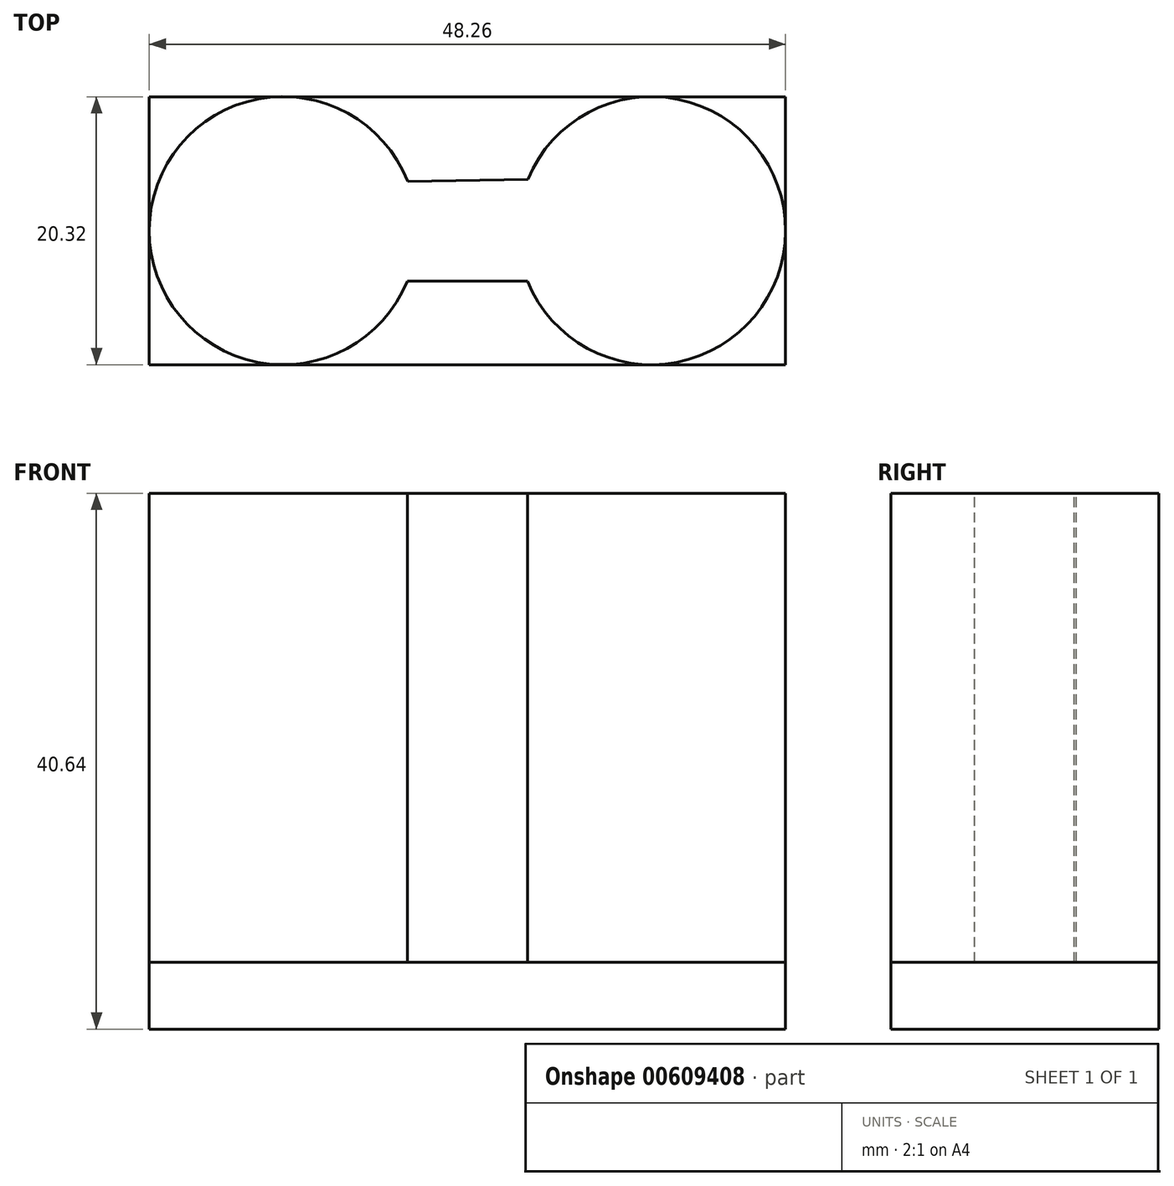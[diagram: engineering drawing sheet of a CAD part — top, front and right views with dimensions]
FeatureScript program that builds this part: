
annotation { "Feature Type Name" : "Feature", "Feature Type Description" : "" }
export const myFeature = defineFeature(function(context is Context, id is Id, definition is map)
    precondition{}
    {
        {
            var Q0;
            Q0=qCreatedBy(makeId("Top.planeOp"),FACE);
            var sketch = newSketch(context, id + "F0", { "sketchPlane" : qUnion([Q0])});
            skLineSegment(sketch, "E0.bottom", {"start": v(0, 0) * mm, "end": v(-48.26, 0) * mm});
            skLineSegment(sketch, "E0.top", {"start": v(0, 20.32) * mm, "end": v(-48.26, 20.32) * mm});
            skLineSegment(sketch, "E0.left", {"start": v(0, 0) * mm, "end": v(0, 20.32) * mm});
            skLineSegment(sketch, "E0.right", {"start": v(-48.26, 0) * mm, "end": v(-48.26, 20.32) * mm});
            skSolve(sketch);
        }
        {
            var Q0;
            Q0 = qSketchRegion(id + "F0", true);
            extrude(context, id + "F1", {"entities" : qUnion([Q0]), "depth" : 40.64 * mm, "offsetDistance" : 25.4 * mm});
        }
        {
            var Q0;
            Q0=makeQuery(id+"F1.opExtrude","CAP_FACE",FACE,{"disambiguationData":[OSD([sQuery(id+"F0.wireOp",EDGE,"E0.bottom"),sQuery(id+"F0.wireOp",EDGE,"E0.top"),sQuery(id+"F0.wireOp",EDGE,"E0.left"),sQuery(id+"F0.wireOp",EDGE,"E0.right")])],"isStart":false});
            var sketch = newSketch(context, id + "F2", { "sketchPlane" : qUnion([Q0])});
            skArc(sketch, "E1", {"start": v(-28.65, 13.9) * mm, "mid": v(-48.26, 10.2) * mm, "end": v(-28.68, 6.35) * mm});
            skArc(sketch, "E2", {"start": v(-19.58, 6.35) * mm, "mid": v(0, 10.12) * mm, "end": v(-19.55, 14.04) * mm});
            skLineSegment(sketch, "E3.trimOffspring", {"start": v(-28.68, 6.35) * mm, "end": v(-19.58, 6.35) * mm});
            skLineSegment(sketch, "E4.trimOffspring", {"start": v(-28.65, 13.9) * mm, "end": v(-19.55, 14.04) * mm});
            skLineSegment(sketch, "E5.bottom", {"start": v(-66.01, 28.5) * mm, "end": v(21.86, 28.5) * mm});
            skLineSegment(sketch, "E5.top", {"start": v(-66.01, -10.25) * mm, "end": v(21.86, -10.25) * mm});
            skLineSegment(sketch, "E5.left", {"start": v(-66.01, 28.5) * mm, "end": v(-66.01, -10.25) * mm});
            skLineSegment(sketch, "E5.right", {"start": v(21.86, 28.5) * mm, "end": v(21.86, -10.25) * mm});
            skSolve(sketch);
        }
        {
            var Q0;
            Q0 = qSketchRegion(id + "F2", true);
            extrude(context, id + "F3", {"entities" : qUnion([Q0]), "operationType" : NewBodyOperationType.REMOVE, "oppositeDirection" : true, "depth" : 35.56 * mm, "offsetDistance" : 25.4 * mm});
        }
    });
